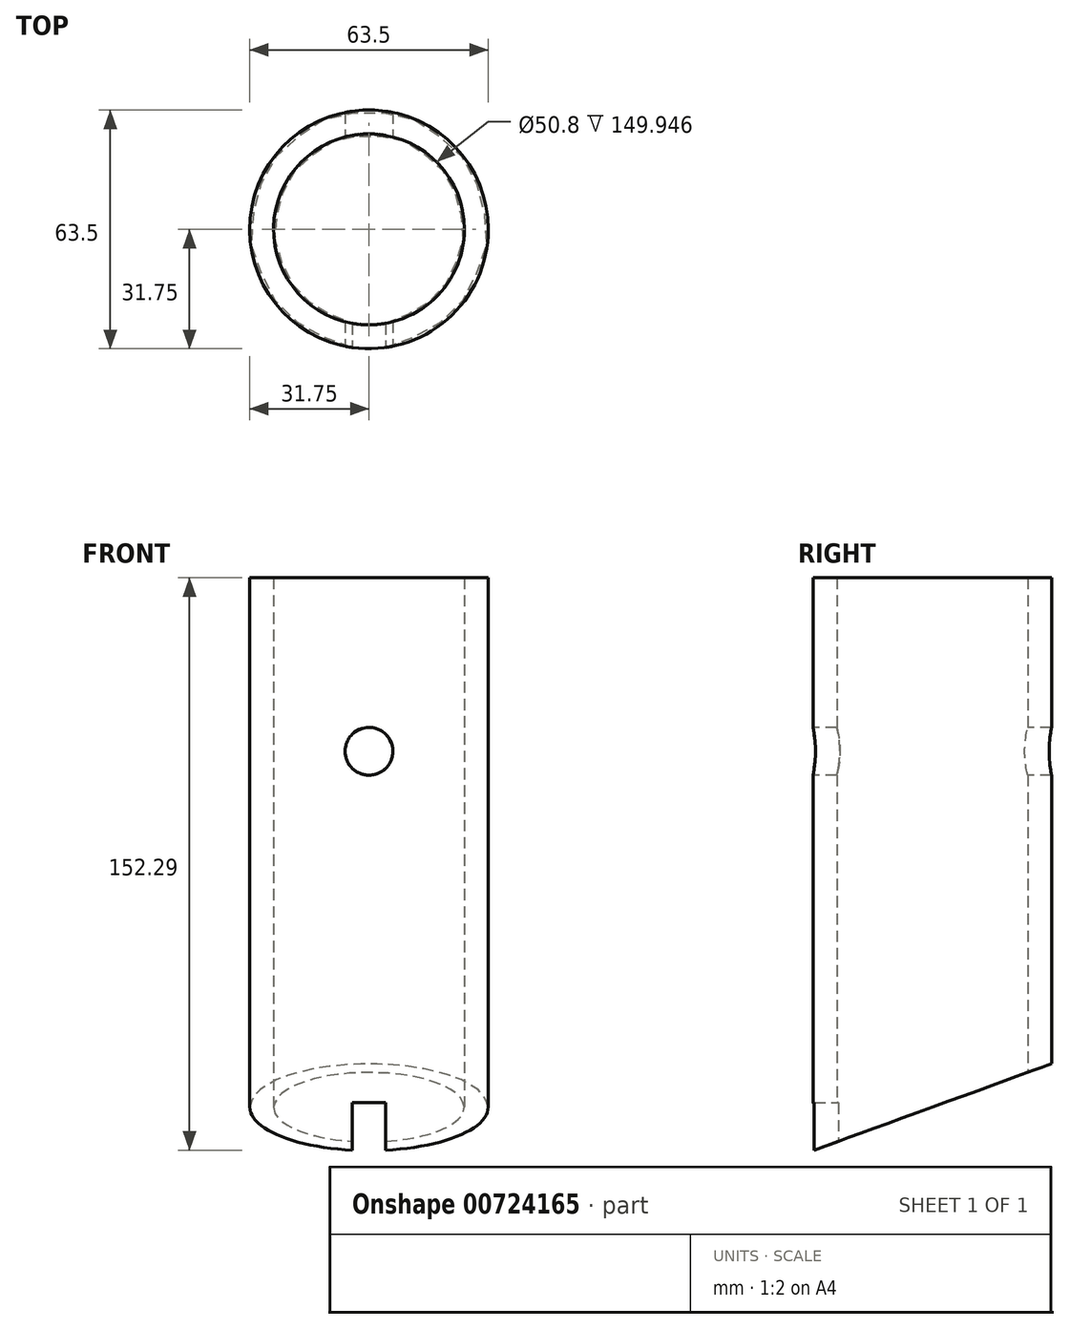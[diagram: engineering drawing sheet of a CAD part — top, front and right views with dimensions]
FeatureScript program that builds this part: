
annotation { "Feature Type Name" : "Feature", "Feature Type Description" : "" }
export const myFeature = defineFeature(function(context is Context, id is Id, definition is map)
    precondition{}
    {
        {
            var Q0;
            Q0=qCreatedBy(makeId("Top.planeOp"),FACE);
            var sketch = newSketch(context, id + "F0", { "sketchPlane" : qUnion([Q0])});
            skCircle(sketch, "E0", {"center": v(0, 0) * mm, "radius": 31.75 * mm});
            skCircle(sketch, "E1", {"center": v(0, 0) * mm, "radius": 25.4 * mm});
            skSolve(sketch);
        }
        {
            var Q0;
            Q0 = qSketchRegion(id + "F0", true);
            extrude(context, id + "F1", {"entities" : qUnion([Q0]), "depth" : 152.4 * mm, "offsetDistance" : 25.4 * mm});
        }
        {
            var Q0;
            Q0=qCreatedBy(makeId("Right.planeOp"),FACE);
            var sketch = newSketch(context, id + "F2", { "sketchPlane" : qUnion([Q0])});
            skLineSegment(sketch, "E2", {"start": v(31.75, 0) * mm, "end": v(-31.75, 0) * mm});
            skLineSegment(sketch, "E3", {"start": v(-31.75, 0) * mm, "end": v(31.75, 23.11) * mm});
            skLineSegment(sketch, "E4", {"start": v(31.75, 23.11) * mm, "end": v(31.75, 0) * mm});
            skSolve(sketch);
        }
        {
            var Q0;
            Q0 = qSketchRegion(id + "F2", true);
            extrude(context, id + "F3", {"entities" : qUnion([Q0]), "operationType" : NewBodyOperationType.REMOVE, "depth" : 63.5 * mm, "offsetDistance" : 25.4 * mm, "symmetric" : true});
        }
        {
            var Q0;
            Q0=qCreatedBy(makeId("Front.planeOp"),FACE);
            var sketch = newSketch(context, id + "F4", { "sketchPlane" : qUnion([Q0])});
            skLineSegment(sketch, "E5", {"start": v(0, 4.65) * mm, "end": v(0, 106.25) * mm, "construction": true});
            skCircle(sketch, "E6", {"center": v(0, 106.25) * mm, "radius": 6.35 * mm});
            skSolve(sketch);
        }
        {
            var Q0;
            Q0 = qSketchRegion(id + "F4", true);
            extrude(context, id + "F5", {"entities" : qUnion([Q0]), "operationType" : NewBodyOperationType.REMOVE, "oppositeDirection" : true, "depth" : 63.5 * mm, "offsetDistance" : 25.4 * mm, "symmetric" : true});
        }
        {
            var Q0;
            Q0=qCreatedBy(makeId("Front.planeOp"),FACE);
            var sketch = newSketch(context, id + "F6", { "sketchPlane" : qUnion([Q0])});
            skLineSegment(sketch, "E7.bottom", {"start": v(4.44, -12.7) * mm, "end": v(-4.45, -12.7) * mm});
            skLineSegment(sketch, "E7.top", {"start": v(4.45, 12.7) * mm, "end": v(-4.44, 12.7) * mm});
            skLineSegment(sketch, "E7.left", {"start": v(4.44, -12.7) * mm, "end": v(4.45, 12.7) * mm});
            skLineSegment(sketch, "E7.right", {"start": v(-4.45, -12.7) * mm, "end": v(-4.44, 12.7) * mm});
            skPoint(sketch, "E7.middle", {"position": v(0, 0) * mm});
            skSolve(sketch);
        }
        {
            var Q0;
            Q0 = qSketchRegion(id + "F6", true);
            extrude(context, id + "F7", {"entities" : qUnion([Q0]), "operationType" : NewBodyOperationType.REMOVE, "depth" : 38.1 * mm, "offsetDistance" : 25.4 * mm});
        }
    });
